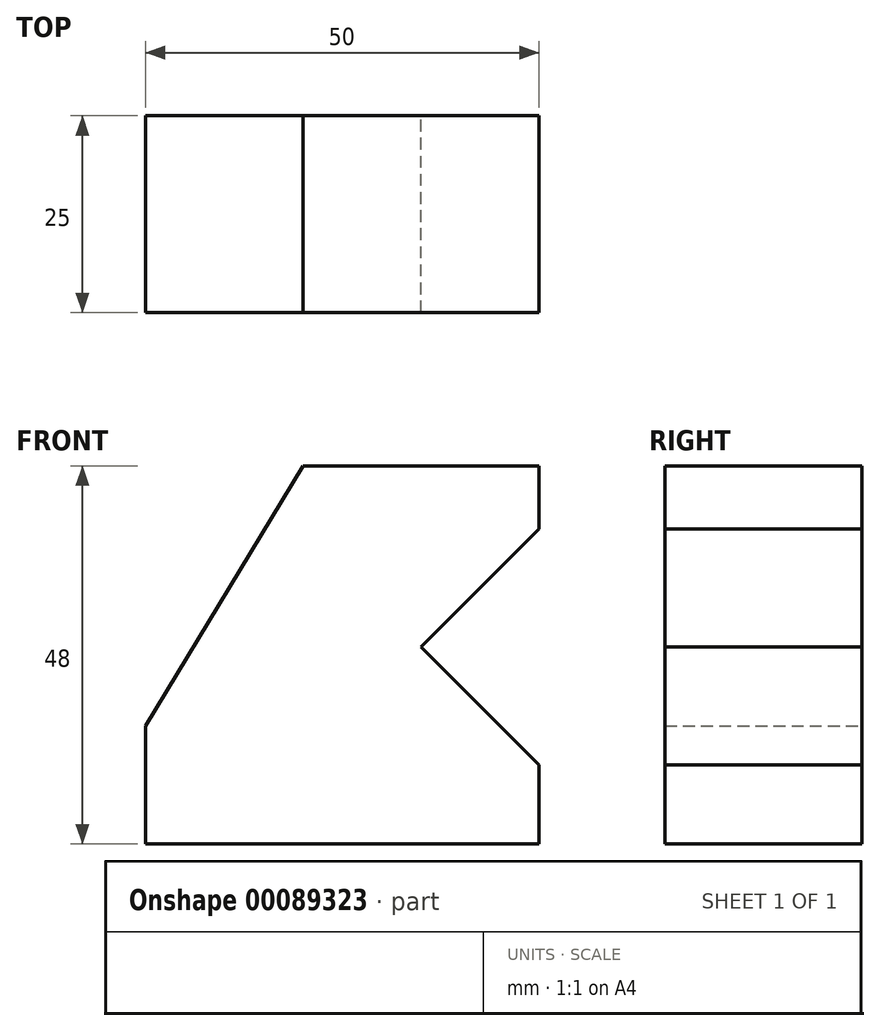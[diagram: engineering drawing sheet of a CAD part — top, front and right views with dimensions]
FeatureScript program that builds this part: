
annotation { "Feature Type Name" : "Feature", "Feature Type Description" : "" }
export const myFeature = defineFeature(function(context is Context, id is Id, definition is map)
    precondition{}
    {
        {
            var Q0;
            Q0=qCreatedBy(makeId("Front.planeOp"),FACE);
            var sketch = newSketch(context, id + "F0", { "sketchPlane" : qUnion([Q0])});
            skLineSegment(sketch, "E0", {"start": v(0, 0) * mm, "end": v(15, 15) * mm});
            skLineSegment(sketch, "E1", {"start": v(0, 0) * mm, "end": v(15, -15) * mm});
            skLineSegment(sketch, "E2", {"start": v(15, -15) * mm, "end": v(15, -25) * mm});
            skLineSegment(sketch, "E3", {"start": v(15, -25) * mm, "end": v(-35, -25) * mm});
            skLineSegment(sketch, "E4", {"start": v(-35, -25) * mm, "end": v(-35, -10) * mm});
            skLineSegment(sketch, "E5", {"start": v(-35, -10) * mm, "end": v(-15, 23) * mm});
            skLineSegment(sketch, "E6", {"start": v(-15, 23) * mm, "end": v(15, 23) * mm});
            skLineSegment(sketch, "E7", {"start": v(15, 23) * mm, "end": v(15, 15) * mm});
            skLineSegment(sketch, "E8", {"start": v(15, -15) * mm, "end": v(15, 44.56) * mm, "construction": true});
            skLineSegment(sketch, "E9", {"start": v(-35.31, 0) * mm, "end": v(45.12, 0) * mm, "construction": true});
            skSolve(sketch);
        }
        {
            var Q0;
            Q0 = qSketchRegion(id + "F0", true);
            extrude(context, id + "F1", {"entities" : qUnion([Q0]), "depth" : 25 * mm});
        }
    });
